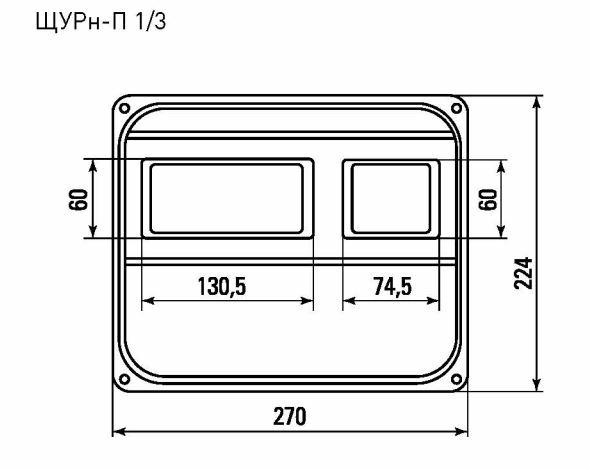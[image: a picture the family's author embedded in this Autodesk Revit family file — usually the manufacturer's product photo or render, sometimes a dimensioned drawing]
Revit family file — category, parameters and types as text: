
# Revit family: EKF_EE_Бокс_Пластиковый_Монтажная_Плата _IP65_PROxima
name_source: partatom
category: Электрооборудование
units: mm (PartAtom-declared; Revit-internal decimal feet)

## family parameters
Всегда вертикально = Да
На основе рабочей плоскости = Нет
Общий = Нет
При загрузке вырезать с полостями = Нет
Размер круглого соединителя = Использовать диаметр
Тип детали = Силовой щит
Точка расчета площади = Да

## types (10) — shared parameters
ADSK_Единица измерения = компл.
ADSK_Завод-изготовитель = EKF
ADSK_Количество = 1
ADSK_Марка = Бокс пластиковый с монтажной платой IP65
ADSK_Материал = RAL 7035_Сталь
ADSK_Обозначение = Бокс пластиковый с монтажной платой IP65
Изготовитель = EKF
Серия номенклатуры = PROxima
Степень защиты IP = IP65
ТВ = EKF
Тип установки = Навесной
zero-valued in all types: Количество DIN-реек, Количество модулей на DIN-рейке, Максимальное количество модулей

## per-type parameters (varying)
| type | ADSK_Код изделия | ADSK_Масса | ADSK_Наименование | ADSK_Размер_Высота | ADSK_Размер_Глубина | ADSK_Размер_Ширина | Описание | Тип |
| Бокс пластиковый с монтажной платой 300х200х130 мм IP65 EKF PROxima | PB65MP001 | 1.4 | Бокс пластиковый с монтажной платой 300х200х130 мм IP65 EKF PROximaБокс пластиковый с монтажной платой 300х200х130 мм IP65 EKF PROxima | 300 мм | 130 мм | 200 мм | Бокс пластиковый с монтажной платой 300х200х130 мм IP65 EKF PROximaБокс пластиковый с монтажной платой 300х200х130 мм IP65 EKF PROxima | 137 мм |
| Бокс пластиковый с монтажной платой 350х250х150 мм IP65 EKF PROxima | PB65MP002 | 2.2 | Бокс пластиковый с монтажной платой 350х250х150 мм IP65 EKF PROximaБокс пластиковый с монтажной платой 350х250х150 мм IP65 EKF PROxima | 350 мм | 150 мм | 250 мм | Бокс пластиковый с монтажной платой 350х250х150 мм IP65 EKF PROximaБокс пластиковый с монтажной платой 350х250х150 мм IP65 EKF PROxima | 138 мм |
| Бокс пластиковый с монтажной платой 400х300х170 мм IP65 EKF PROxima | PB65MP003 | 2.9 | Бокс пластиковый с монтажной платой 400х300х170 мм IP65 EKF PROximaБокс пластиковый с монтажной платой 400х300х170 мм IP65 EKF PROxima | 400 мм | 170 мм | 300 мм | Бокс пластиковый с монтажной платой 400х300х170 мм IP65 EKF PROximaБокс пластиковый с монтажной платой 400х300х170 мм IP65 EKF PROxima | 139 мм |
| Бокс пластиковый с монтажной платой 400х300х220 мм IP65 EKF PROxima | PB65MP004 | 3.2 | Бокс пластиковый с монтажной платой 400х300х220 мм IP65 EKF PROximaБокс пластиковый с монтажной платой 400х300х220 мм IP65 EKF PROxima | 400 мм | 220 мм | 300 мм | Бокс пластиковый с монтажной платой 400х300х220 мм IP65 EKF PROximaБокс пластиковый с монтажной платой 400х300х220 мм IP65 EKF PROxima | 140 мм |
| Бокс пластиковый с монтажной платой 500х350х190 мм IP65 EKF PROxima | PB65MP005 | 4 | Бокс пластиковый с монтажной платой 500х350х190 мм IP65 EKF PROximaБокс пластиковый с монтажной платой 500х350х190 мм IP65 EKF PROxima | 500 мм | 190 мм | 350 мм | Бокс пластиковый с монтажной платой 500х350х190 мм IP65 EKF PROximaБокс пластиковый с монтажной платой 500х350х190 мм IP65 EKF PROxima | 141 мм |
| Бокс пластиковый с монтажной платой 500х400х180 мм IP65 EKF PROxima | PB65MP006 | 4.3 | Бокс пластиковый с монтажной платой 500х400х180 мм IP65 EKF PROximaБокс пластиковый с монтажной платой 500х400х180 мм IP65 EKF PROxima | 500 мм | 180 мм | 400 мм | Бокс пластиковый с монтажной платой 500х400х180 мм IP65 EKF PROximaБокс пластиковый с монтажной платой 500х400х180 мм IP65 EKF PROxima | 142 мм |
| Бокс пластиковый с монтажной платой 500х400х240 мм IP65 EKF PROxima | PB65MP007 | 4.9 | Бокс пластиковый с монтажной платой 500х400х240 мм IP65 EKF PROximaБокс пластиковый с монтажной платой 500х400х240 мм IP65 EKF PROxima | 500 мм | 240 мм | 400 мм | Бокс пластиковый с монтажной платой 500х400х240 мм IP65 EKF PROximaБокс пластиковый с монтажной платой 500х400х240 мм IP65 EKF PROxima | 143 мм |
| Бокс пластиковый с монтажной платой 600х400х200 мм IP65 EKF PROxima | PB65MP008 | 5.2 | Бокс пластиковый с монтажной платой 600х400х200 мм IP65 EKF PROximaБокс пластиковый с монтажной платой 600х400х200 мм IP65 EKF PROxima | 600 мм | 200 мм | 400 мм | Бокс пластиковый с монтажной платой 600х400х200 мм IP65 EKF PROximaБокс пластиковый с монтажной платой 600х400х200 мм IP65 EKF PROxima | 144 мм |
| Бокс пластиковый с монтажной платой 700х500х250 мм IP65 EKF PROxima | PB65MP009 | 8.3 | Бокс пластиковый с монтажной платой 700х500х250 мм IP65 EKF PROximaБокс пластиковый с монтажной платой 700х500х250 мм IP65 EKF PROxima | 700 мм | 250 мм | 500 мм | Бокс пластиковый с монтажной платой 700х500х250 мм IP65 EKF PROximaБокс пластиковый с монтажной платой 700х500х250 мм IP65 EKF PROxima | 145 мм |
| Бокс пластиковый с монтажной платой 800х600х260 мм IP65 EKF PROxima | PB65MP010 | 13.1 | Бокс пластиковый с монтажной платой 800х600х260 мм IP65 EKF PROximaБокс пластиковый с монтажной платой 800х600х260 мм IP65 EKF PROxima | 800 мм | 260 мм | 600 мм | Бокс пластиковый с монтажной платой 800х600х260 мм IP65 EKF PROximaБокс пластиковый с монтажной платой 800х600х260 мм IP65 EKF PROxima | 146 мм |
